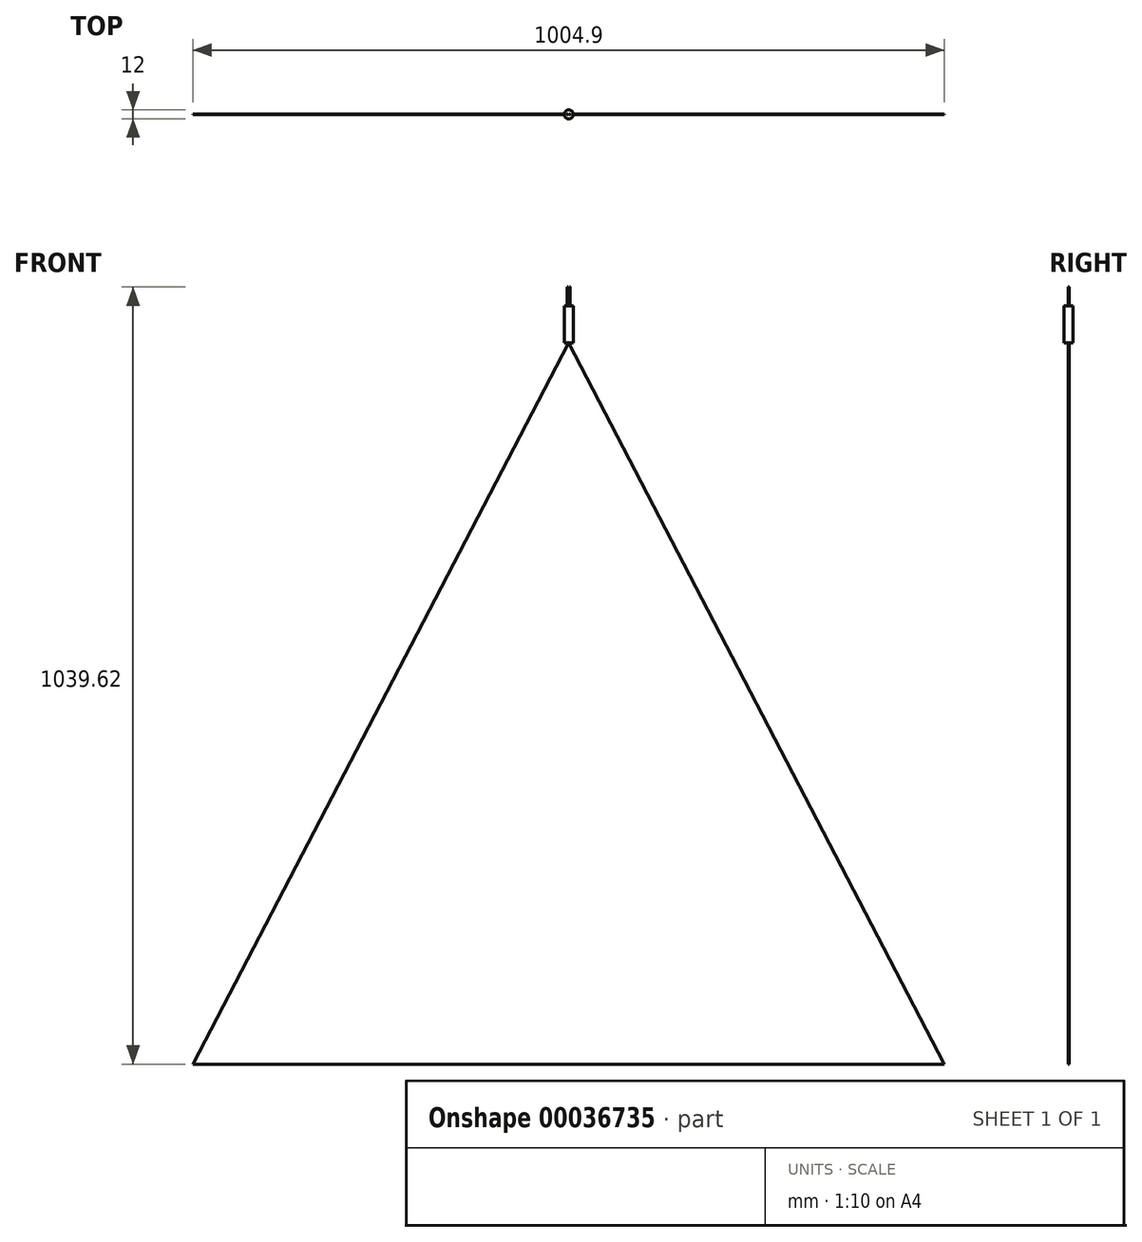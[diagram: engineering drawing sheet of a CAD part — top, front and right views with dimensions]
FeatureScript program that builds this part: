
annotation { "Feature Type Name" : "Feature", "Feature Type Description" : "" }
export const myFeature = defineFeature(function(context is Context, id is Id, definition is map)
    precondition{}
    {
        {
            var Q0;
            Q0=qCreatedBy(makeId("Top.planeOp"),FACE);
            var sketch = newSketch(context, id + "F0", { "sketchPlane" : qUnion([Q0])});
            skCircle(sketch, "E0", {"center": v(0, 0) * mm, "radius": 6 * mm});
            skSolve(sketch);
        }
        {
            var Q0;
            Q0=makeQuery(id+"F0.imprint","IMPRINT",FACE,{"disambiguationData":[TD([[makeQuery(id+"F0.imprint","IMPRINT",EDGE,{"derivedFrom":sQuery(id+"F0.wireOp",EDGE,"E0")}),1.0]])]});
            extrude(context, id + "F1", {"entities" : qUnion([Q0]), "depth" : 49.02 * mm, "offsetDistance" : 25.4 * mm});
        }
        {
            var Q0;
            Q0=makeQuery(id+"F1.opExtrude","CAP_FACE",FACE,{"disambiguationData":[OSD([sQuery(id+"F0.wireOp",EDGE,"E0")])],"isStart":false});
            var sketch = newSketch(context, id + "F2", { "sketchPlane" : qUnion([Q0])});
            skCircle(sketch, "E1", {"center": v(-1.52, 0) * mm, "radius": 0.5 * mm});
            skSolve(sketch);
        }
        {
            var Q0;
            Q0=makeQuery(id+"F2.imprint","IMPRINT",FACE,{"disambiguationData":[TD([[makeQuery(id+"F2.imprint","IMPRINT",EDGE,{"derivedFrom":sQuery(id+"F2.wireOp",EDGE,"E1")}),1.0]])]});
            extrude(context, id + "F3", {"entities" : qUnion([Q0]), "depth" : 25.4 * mm});
        }
        {
            var Q0;
            Q0=makeQuery(id+"F1.opExtrude","CAP_FACE",FACE,{"disambiguationData":[OSD([sQuery(id+"F0.wireOp",EDGE,"E0")])],"isStart":false});
            var sketch = newSketch(context, id + "F4", { "sketchPlane" : qUnion([Q0])});
            skCircle(sketch, "E2", {"center": v(1.52, 0) * mm, "radius": 0.5 * mm});
            skSolve(sketch);
        }
        {
            var Q0;
            Q0=makeQuery(id+"F4.imprint","IMPRINT",FACE,{"disambiguationData":[TD([[makeQuery(id+"F4.imprint","IMPRINT",EDGE,{"derivedFrom":sQuery(id+"F4.wireOp",EDGE,"E2")}),1.0]])]});
            extrude(context, id + "F5", {"entities" : qUnion([Q0]), "depth" : 25.4 * mm});
        }
        {
            var Q0;
            Q0=qCreatedBy(makeId("Front.planeOp"),FACE);
            var sketch = newSketch(context, id + "F6", { "sketchPlane" : qUnion([Q0])});
            skLineSegment(sketch, "E3", {"start": v(0, 0) * mm, "end": v(502.45, -965.2) * mm});
            skLineSegment(sketch, "E4", {"start": v(502.45, -965.2) * mm, "end": v(-502.45, -965.2) * mm});
            skLineSegment(sketch, "E5", {"start": v(-502.45, -965.2) * mm, "end": v(0, 0) * mm});
            skSolve(sketch);
        }
        {
            var Q0;
            Q0=makeQuery(id+"F6.imprint","IMPRINT",FACE,{"disambiguationData":[TD([[makeQuery(id+"F6.imprint","IMPRINT",EDGE,{"derivedFrom":sQuery(id+"F6.wireOp",EDGE,"E3")}),-1.0]])]});
            extrude(context, id + "F7", {"entities" : qUnion([Q0]), "endBound" : BoundingType.SYMMETRIC, "depth" : 1 * mm});
        }
        {
            var Q0;
            Q0=makeQuery(id+"F7.opExtrude","CAP_FACE",FACE,{"disambiguationData":[OSD([sQuery(id+"F6.wireOp",EDGE,"E3"),sQuery(id+"F6.wireOp",EDGE,"E4"),sQuery(id+"F6.wireOp",EDGE,"E5")])],"isStart":false});
            var sketch = newSketch(context, id + "F8", { "sketchPlane" : qUnion([Q0])});
            skLineSegment(sketch, "E6", {"start": v(-536.96, -670.08) * mm, "end": v(108.48, 0) * mm});
            skLineSegment(sketch, "E7", {"start": v(108.48, 0) * mm, "end": v(858.4, -722.34) * mm});
            skLineSegment(sketch, "E8", {"start": v(858.4, -722.34) * mm, "end": v(-536.96, -670.08) * mm});
            skSolve(sketch);
        }
        {
            var Q0;
            {var subQ7=sQuery(id+"F8.wireOp",EDGE,"E7");Q0=makeQuery(id+"F8.imprint","IMPRINT",FACE,{"disambiguationData":[TD([[makeQuery(id+"F8.imprint","IMPRINT",EDGE,{"derivedFrom":subQ7}),-1.0]])]});}
            extrude(context, id + "F9", {"entities" : qUnion([Q0]), "operationType" : NewBodyOperationType.REMOVE, "endBound" : BoundingType.THROUGH_ALL, "oppositeDirection" : true, "depth" : 25.4 * mm});
        }
        {
            var Q0;
            Q0=makeQuery(id+"F7.opExtrude","CAP_FACE",FACE,{"disambiguationData":[OSD([sQuery(id+"F6.wireOp",EDGE,"E3"),sQuery(id+"F6.wireOp",EDGE,"E4"),sQuery(id+"F6.wireOp",EDGE,"E5")])],"isStart":false});
            var sketch = newSketch(context, id + "F10", { "sketchPlane" : qUnion([Q0])});
            skLineSegment(sketch, "E9", {"start": v(-639.64, -762.8) * mm, "end": v(202.66, 133.93) * mm});
            skLineSegment(sketch, "E10", {"start": v(202.66, 133.93) * mm, "end": v(1032.8, -741.94) * mm});
            skLineSegment(sketch, "E11", {"start": v(1032.8, -741.94) * mm, "end": v(-639.64, -762.8) * mm});
            skSolve(sketch);
        }
        {
            var Q0;
            {var subQ0=makeQuery(id+"F7.opExtrude","CAP_EDGE",EDGE,{"disambiguationData":[OSD([sQuery(id+"F6.wireOp",EDGE,"E4")])],"isStart":false});var subQ1=sQuery(id+"F10.wireOp",EDGE,"E9");var subQ2=makeQuery(id+"F10.imprint","INTERSECT",VERTEX,{"derivedFrom":[subQ0,subQ1]});Q0=makeQuery(id+"F10.imprint","IMPRINT",FACE,{"disambiguationData":[TD([[makeQuery(id+"F10.imprint","IMPRINT",EDGE,{"disambiguationData":[TD([[subQ2,-1.0]])],"derivedFrom":subQ1}),-1.0]])]});}
            extrude(context, id + "F11", {"entities" : qUnion([Q0]), "operationType" : NewBodyOperationType.REMOVE, "endBound" : BoundingType.THROUGH_ALL, "oppositeDirection" : true, "depth" : 25.4 * mm});
        }
    });
